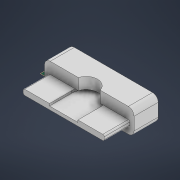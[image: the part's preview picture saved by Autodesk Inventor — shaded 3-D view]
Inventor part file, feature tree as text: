
AUTODESK INVENTOR PART (.ipt)
format: ipt  version: 2022 (Build 260153000, 153)  size: 457,216 bytes
history: native  units: mm
features: sketch x7, extrude x6, fillet x2, emboss x1, plane x1
ambient origin geometry x8: Origin, YZ Plane, XZ Plane, XY Plane, X Axis, Y Axis, Z Axis, Center Point
bodies: Solid1 (feature_tree)
feature tree (17):
  extrude  "Extrusion1"  Depth=17.0mm
  extrude  "10 mL cross"  Depth=8.0mm TaperAngle=0.0deg
  extrude  "10 mL top"  Depth=8.0mm TaperAngle=0.0deg
  extrude  "Extrusion4"  Depth=63.0mm
  emboss  "Emboss1"
  plane  "Work Plane1"
  extrude  "Extrusion8"  Depth=1.0mm
  extrude  "Extrusion10"  Depth=5.2mm
  fillet  "Fillet5"  Radius=3.0mm
  fillet  "Fillet6"  Radius=18.0mm
  sketch  "Sketch1"  dims[d0=63.0mm d1=17.0mm]
  sketch  "Sketch2"  dims[d2=35.0mm d3=0.0mm d5=8.0mm d6=0.0mm]
  sketch  "Sketch3"  dims[d8=1.5mm d9=0.0mm d11=8.0mm d12=0.0mm]
  sketch  "Sketch4"  dims[d19=63.0mm d20=18.0mm]
  sketch  "Sketch10"  dims[d33=1.0mm d34=0.0mm d41=18.0mm]
  sketch  "Sketch11"  dims[d42=5.2mm d43=0.0mm d52=3.0mm d53=3.0mm d54=18.0mm d55=0.0mm]
  sketch  "Sketch13"  dims[d64=1.0mm d65=4.0mm d66=15.75mm d67=16.0mm d68=20.0mm d69=15.75mm d51=0.5mm]
